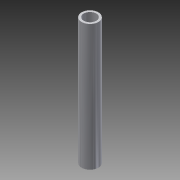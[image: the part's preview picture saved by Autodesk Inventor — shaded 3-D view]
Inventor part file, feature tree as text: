
AUTODESK INVENTOR PART (.ipt)
format: ipt  version: 2015 (Build 190159000, 159)  size: 91,136 bytes
history: native  units: mm
features: extrude x2, sketch x2, other x1
ambient origin geometry x8: Origin, YZ Plane, XZ Plane, XY Plane, X Axis, Y Axis, Z Axis, Center Point
bodies: Body1 (feature_tree)
feature tree (5):
  other  "ソリッド1"
  extrude  "押し出し1"  Depth=4.0mm
  extrude  "押し出し2"  Depth=30.0mm TaperAngle=0.0deg
  sketch  "スケッチ1"
  sketch  "スケッチ2"
